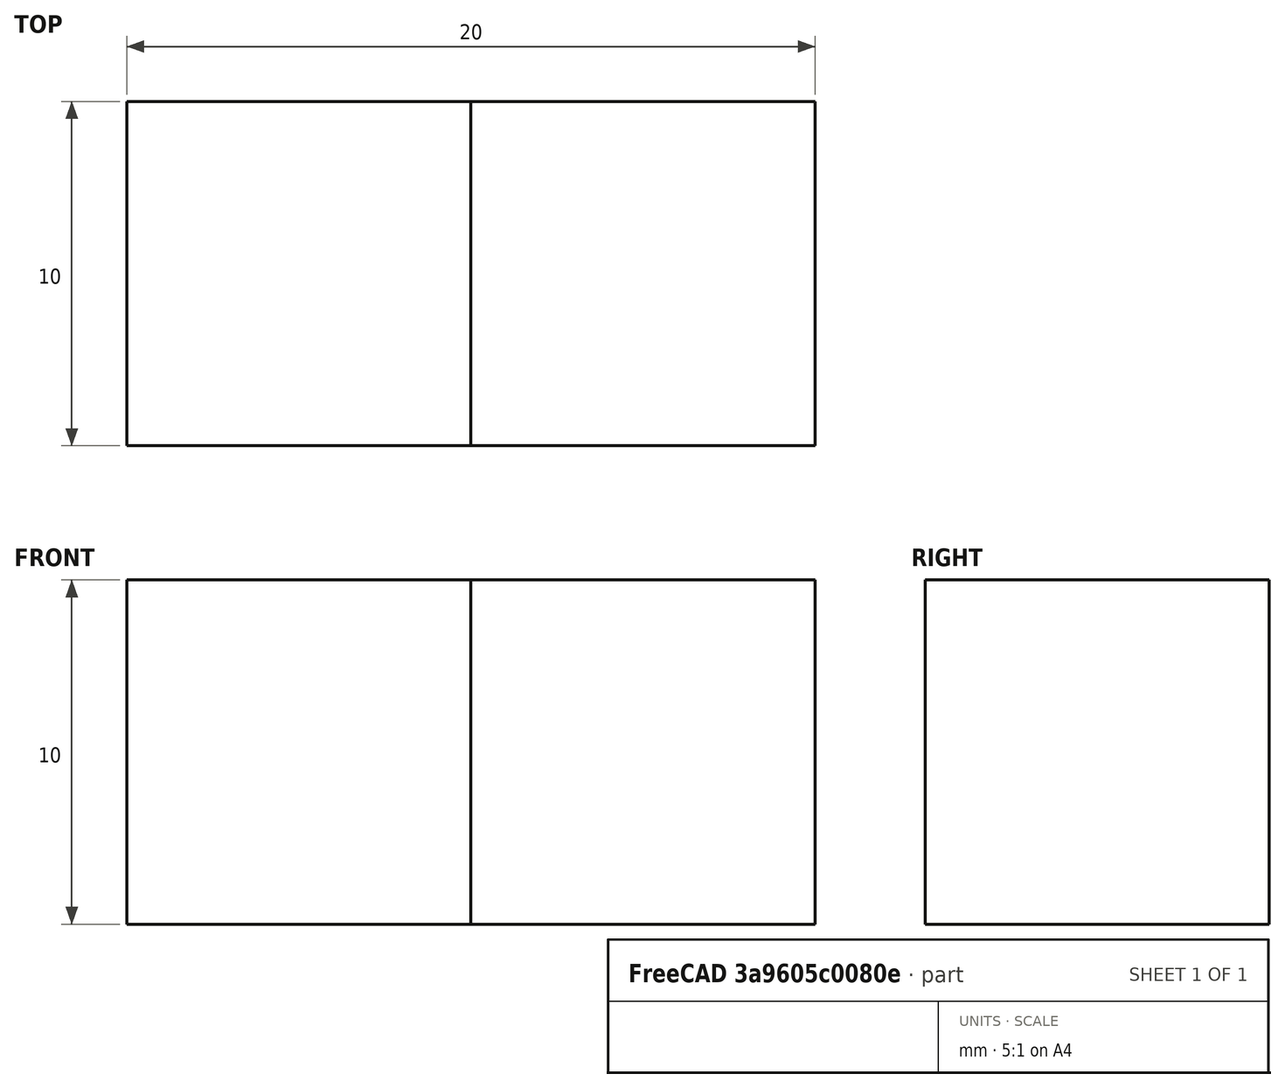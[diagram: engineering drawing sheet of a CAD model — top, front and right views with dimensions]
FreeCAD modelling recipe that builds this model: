
FCSTD DOCUMENT  (FreeCAD 0.21R33694 (Git))
Label: VM_Uniaxial_Tension_Example
License: All rights reserved
LicenseURL: http://en.wikipedia.org/wiki/All_rights_reserved
objects: Fem::ConstraintDisplacement×3, Part::Box×2, App::MaterialObjectPython×2, Fem::FemSolverObjectPython×1, Part::FeaturePython×1, Fem::ConstraintPressure×1, Fem::FemMeshShapeNetgenObject×1, Fem::FemMeshObjectPython×1, Fem::FemResultObjectPython×1, Fem::FemAnalysis×1
note: 3 computed .brp shape members not serialized (recipe doc carries the construction recipe); baked Part::Feature solids carry a one-line shape summary decoded from their .brp

FEATURE [Part::Box] Box  label="Cube"
  AttacherType = Attacher::AttachEngine3D
  Height = 10
  Length = 10
  Width = 10
FEATURE [Fem::FemSolverObjectPython] SolverCcxTools  # FEM object (typed FeaturePython)
  AnalysisType = 0
  BeamShellResultOutput3D = false
  BucklingFactors = 1
  EigenmodeHighLimit = 1000000
  EigenmodeLowLimit = 0
  EigenmodesCount = 10
  GeometricalNonlinearity = 0
  IterationsControlParameterCutb = 0.25,0.5,0.75,0.85,,,1.5,
  IterationsControlParameterIter = 4,8,9,200,10,400,,200,,
  IterationsControlParameterTimeUse = false
  IterationsThermoMechMaximum = 2000
  IterationsUserDefinedIncrementations = false
  IterationsUserDefinedTimeStepLength = false
  MaterialNonlinearity = 0
  MatrixSolverType = 0
  SplitInputWriter = false
  ThermoMechSteadyState = true
  TimeEnd = 1
  TimeInitialStep = 0.01
FEATURE [Part::Box] Box001  label="Cube001"
  AttacherType = Attacher::AttachEngine3D
  Height = 10
  Length = 10
  Placement = pos=(10,0,0) rot=(0,0,1;0rad)
  Width = 10
FEATURE [Part::FeaturePython] BooleanFragments  # WARN: FeaturePython — macro-defined, semantics opaque (R4)
  Mode = 2
  Objects = -> [Box,Box001]
  Tolerance = 0
FEATURE [Fem::ConstraintDisplacement] ConstraintDisplacement
  NormalDirection = (0,0,-1)
  Normals = (18) [(0,0,-1),(0,0,-1),(0,0,-1),(0,0,-1),(0,0,-1),(0,0,-1),(0,0,-1),(0,0,-1),(0,0,-1),(0,0,-1),(0,0,-1),(0,0,-1),(0,0,-1),(0,0,-1),(0,0,-1),(0,0,-1),+2 more]
  Points = (18) [(0,0,0),(5,0,0),(10,0,0),(0,5,0),(5,5,0),(10,5,0),(0,10,0),(5,10,0),(10,10,0),(10,0,0),(15,0,0),(20,0,0),(10,5,0),(15,5,0),(20,5,0),(10,10,0),+2 more]
  References = -> [BooleanFragments]
  hasXFormula = false
  hasYFormula = false
  hasZFormula = false
  rotxFix = false
  rotxFree = true
  rotyFix = false
  rotyFree = true
  rotzFix = false
  rotzFree = true
  useFlowSurfaceForce = false
  xDisplacement = 0
  xFix = false
  xFree = true
  xRotation = 0
  yDisplacement = 0
  yFix = false
  yFree = true
  yRotation = 0
  zDisplacement = 0
  zFix = true
  zFree = false
  zRotation = 0
FEATURE [Fem::ConstraintDisplacement] ConstraintDisplacement001
  NormalDirection = (-1,0,0)
  Normals = (9) [(-1,0,0),(-1,0,0),(-1,0,0),(-1,0,0),(-1,0,0),(-1,0,0),(-1,0,0),(-1,0,0),(-1,0,0)]
  Points = (9) [(0,10,0),(0,10,5),(0,10,10),(0,5,0),(0,5,5),(0,5,10),(0,0,0),(0,0,5),(0,0,10)]
  References = -> [BooleanFragments]
  hasXFormula = false
  hasYFormula = false
  hasZFormula = false
  rotxFix = false
  rotxFree = true
  rotyFix = false
  rotyFree = true
  rotzFix = false
  rotzFree = true
  useFlowSurfaceForce = false
  xDisplacement = 0
  xFix = true
  xFree = false
  xRotation = 0
  yDisplacement = 0
  yFix = false
  yFree = true
  yRotation = 0
  zDisplacement = 0
  zFix = false
  zFree = true
  zRotation = 0
FEATURE [Fem::ConstraintDisplacement] ConstraintDisplacement002
  NormalDirection = (0,1,0)
  Normals = (18) [(0,1,0),(0,1,0),(0,1,0),(0,1,0),(0,1,0),(0,1,0),(0,1,0),(0,1,0),(0,1,0),(0,1,0),(0,1,0),(0,1,0),(0,1,0),(0,1,0),(0,1,0),(0,1,0),(0,1,0),(0,1,0)]
  Points = (18) [(0,10,0),(0,10,5),(0,10,10),(5,10,0),(5,10,5),(5,10,10),(10,10,0),(10,10,5),(10,10,10),(10,10,0),(10,10,5),(10,10,10),(15,10,0),(15,10,5),(15,10,10),+3 more]
  References = -> [BooleanFragments]
  hasXFormula = false
  hasYFormula = false
  hasZFormula = false
  rotxFix = false
  rotxFree = true
  rotyFix = false
  rotyFree = true
  rotzFix = false
  rotzFree = true
  useFlowSurfaceForce = false
  xDisplacement = 0
  xFix = false
  xFree = true
  xRotation = 0
  yDisplacement = 0
  yFix = true
  yFree = false
  yRotation = 0
  zDisplacement = 0
  zFix = false
  zFree = true
  zRotation = 0
FEATURE [Fem::ConstraintPressure] ConstraintPressure  label="ConstraintPressure(p)"
  NormalDirection = (0,0,1)
  Normals = (18) [(0,0,1),(0,0,1),(0,0,1),(0,0,1),(0,0,1),(0,0,1),(0,0,1),(0,0,1),(0,0,1),(0,0,1),(0,0,1),(0,0,1),(0,0,1),(0,0,1),(0,0,1),(0,0,1),(0,0,1),(0,0,1)]
  Points = (18) [(0,0,10),(5,0,10),(10,0,10),(0,5,10),(5,5,10),(10,5,10),(0,10,10),(5,10,10),(10,10,10),(10,0,10),(15,0,10),(20,0,10),(10,5,10),(15,5,10),(20,5,10),+3 more]
  Pressure = 10
  References = -> [BooleanFragments]
  Reversed = true
FEATURE [App::MaterialObjectPython] MaterialSolid  # material (typed FeaturePython)
  Category = 0
  Material = AuthorAndLicense=(c) 2013 Yorik van Havre (CC-BY 3.0),CardName=Concrete-Generic,CompressiveStrength=25 MPa,Density=2400 kg/m^3,+7 more (map truncated)
  References = -> [BooleanFragments]
FEATURE [App::MaterialObjectPython] MaterialSolid001  # material (typed FeaturePython)
  Category = 0
  Material = AuthorAndLicense=(c) 2014 M. Münch - GNU Lesser General Public License (LGPL),CardName=Steel-S550MC,Density=7800 kg/m^3,+15 more (map truncated)
  References = -> [BooleanFragments]
FEATURE [Fem::FemMeshShapeNetgenObject] FEMMeshNetgen
  Fineness = 0
  GrowthRate = 0.3
  MaxSize = 100
  NbSegsPerEdge = 1
  NbSegsPerRadius = 2
  Optimize = true
  SecondOrder = true
  Shape = -> BooleanFragments
FEATURE [Fem::FemMeshObjectPython] Result_Mesh_Volume  # FEM object (typed FeaturePython)
FEATURE [Fem::FemResultObjectPython] ResultMechanical  # FEM object (typed FeaturePython)
  CriticalStrainRatio = [0,0,0,0,0,0,0,0,0,0,0,0,0,0,0,0,0,0,0,0,0,0,0,0,0,0,0,0,0,0,0,0,0,0,0,0,0,0,0,0,0,0,0,0]
  DisplacementLengths = [1.88048e-05,0.000446384,2.2111e-05,0.000450999,2.08672e-05,0.000590308,0.000598251,2.56861e-05,0,0.000806838,2.87377e-06,0.000838838,0.000594129,0.000493863,0.000448371,0.000499073,2.29209e-05,2.16818e-05,2.16783e-05,2.29089e-05,+24 more]
  DisplacementVectors = (44) [(-1.88048e-05,0,0),(3.808e-05,0,0.000444757),(-2.20954e-05,-8.31322e-07,0),(4.34943e-05,2.77893e-06,0.000448889),(-2.08672e-05,0,0),+39 more]
  Eigenmode = 0
  EigenmodeFrequency = 0
  Mesh = -> Result_Mesh_Volume
  NodeNumbers = [1,2,3,4,5,6,7,8,9,10,11,12,13,14,15,16,17,18,19,20,21,22,23,24,25,26,27,28,29,30,31,32,33,34,35,36,37,38,39,40,41,42,43,44]
  NodeStressXX = [0.287293,-0.459225,0.0517554,-0.237694,-0.324405,0.0174181,0.215531,0.0135247,-0.443956,0.528284,-0.554048,1.03998,0.116475,-0.220904,-0.34846,-0.0110815,-0.15544,-0.0185563,0.169524,0.0326401,-0.0859665,-0.153494,-0.0929692,0.114528,+20 more]
  NodeStressXY = [-0.00938287,-0.00423301,-0.00800667,0.0134398,-0.00284467,0.0177949,0.00224017,-0.0209008,0.00277097,-0.00486984,0.0142551,-0.00406674,0.0100175,0.00678095,0.0046034,0.00783999,-0.0118727,-0.00611377,-0.00869477,-0.0144537,-0.00680794,+23 more]
  NodeStressXZ = [0.0402292,0.463458,0.0597621,0.372041,-0.181557,-0.393853,-0.389234,-0.101771,0.010093,0.0826006,0.00623297,0.0925548,-0.391543,0.0348027,0.41775,-0.00859615,-0.141664,-0.0706639,0.0499956,-0.0210044,0.251844,-0.287705,0.215902,-0.245502,+20 more]
  NodeStressYY = [0.0328866,-0.112442,-0.00558309,-0.00552982,-0.0110011,0.00617214,0.022916,-0.0341939,0.0372539,-0.0128344,0.0115942,-0.007961,0.0145441,-0.0531351,-0.058986,0.00869307,-0.0225975,0.0109428,0.0136518,-0.0198885,-0.0397778,-0.00241448,+22 more]
  NodeStressYZ = [-0.0457458,-0.0201793,-0.00242358,-0.0643497,0.00992476,-0.011874,0.0268803,0.0364876,-0.00287274,-0.000496234,-0.018283,-0.0120277,0.00750315,-0.0160266,-0.0422645,-0.0187347,0.0232062,-0.0179105,-0.0240847,0.017032,-0.0329625,+23 more]
  NodeStressZZ = [19.447,19.5567,19.1945,19.3773,19.6981,20.377,20.2106,20.8637,19.731,20.6162,20.309,20.0805,20.2938,19.9669,19.467,19.794,20.2809,19.5726,19.3208,20.0291,19.5019,20.0375,19.2859,20.5372,20.3483,20.4966,20.1456,20.02,19.7146,20.5864,20.1736,+13 more]
  Peeq = [0,0,0,0,0,0,0,0,0,0,0,0,0,0,0,0,0,0,0,0,0,0,0,0,0,0,0,0,0,0,0,0,0,0,0,0,0,0,0,0,0,0,0,0]
  PrincipalMax = [0.880153,0,0.0484717,0.453801,0.00540654,0.358411,0.475561,0.231945,0.400809,0,0.300836,0.0813347,0.170584,0,0,0.352677,0.12336,0.227395,0.464312,0.115973,0,0.0603526,0.251136,0.353753,0.00332572,0.0931652,0.15817,0.350079,0.166606,0,+14 more]
  PrincipalMin = [195.33,200.246,192.567,198.137,198.112,207.827,206.267,210.019,197.341,206.99,203.272,201.851,206.778,199.766,199.117,198.213,204.44,196.611,193.948,200.671,197.867,203.262,195.352,208.143,204.422,206.584,203.013,200.306,197.372,206.031,+14 more]
  ResultType = Fem::ResultMechanical
  Stats = [-2.55949e-05,5.68277e-05,-2.87377e-06,2.77893e-06,0,0.000843941,0,0.000844568,0,11.366,0,0.880153,0,0,192.567,210.019,0,0,0,0,0,0,0,0,0,0]
  Temperature = [0,0,0,0,0,0,0,0,0,0,0,0,0,0,0,0,0,0,0,0,0,0,0,0,0,0,0,0,0,0,0,0,0,0,0,0,0,0,0,0,0,0,0,0]
  Time = 0
  vonMises = [3.36905,0.0515203,1.19524,1.20908,0,4.29066,6.02524,1.36196,0,6.12921,0,11.366,5.18035,0,0.663511,0.0535466,0,0.459938,2.28214,0.680982,1.72684,1.41687,1.20216,3.6936,8.76178,4.3494,7.77008,0,0,0,0.895603,2.87265,0,1.96321,3.33373,0.263679,+8 more]
FEATURE [Fem::FemAnalysis] Analysis
  Group = -> [SolverCcxTools,ConstraintDisplacement,ConstraintDisplacement001,ConstraintDisplacement002,ConstraintPressure,MaterialSolid,MaterialSolid001,FEMMeshNetgen,ResultMechanical]
